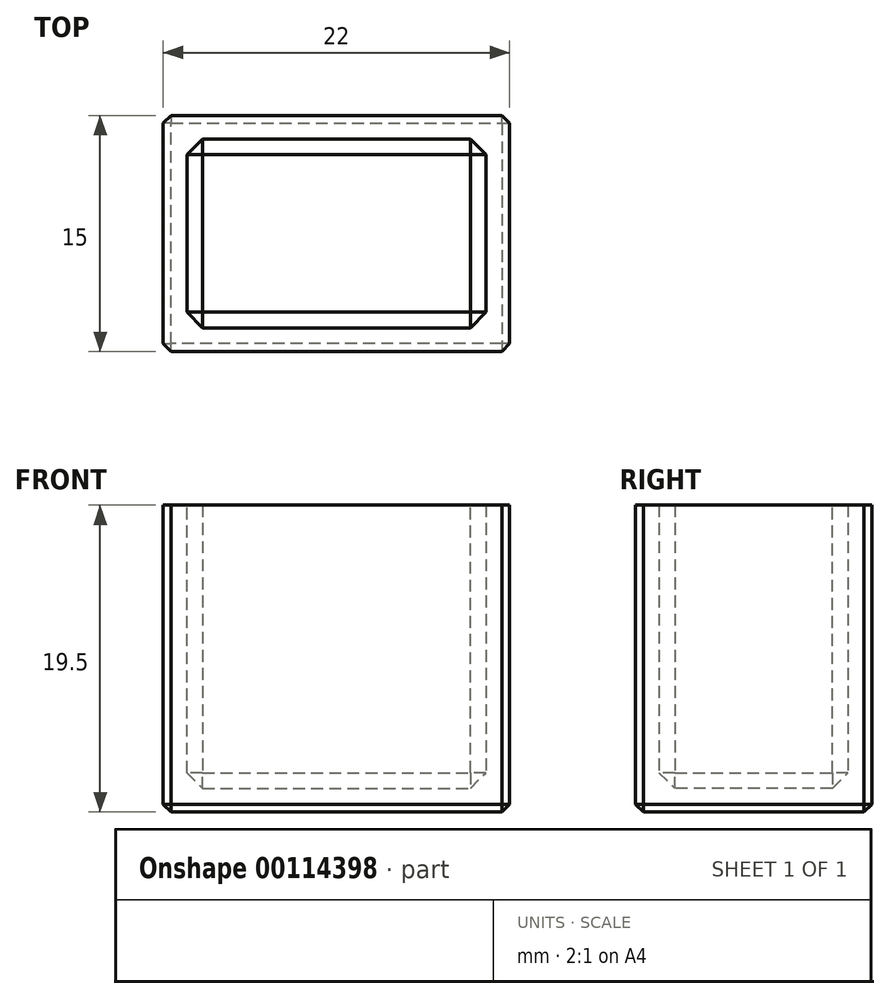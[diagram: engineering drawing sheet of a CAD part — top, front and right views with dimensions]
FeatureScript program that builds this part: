
annotation { "Feature Type Name" : "Feature", "Feature Type Description" : "" }
export const myFeature = defineFeature(function(context is Context, id is Id, definition is map)
    precondition{}
    {
        {
            var Q0;
            Q0=qCreatedBy(makeId("Top.planeOp"),FACE);
            var sketch = newSketch(context, id + "F0", { "sketchPlane" : qUnion([Q0])});
            skLineSegment(sketch, "E0.bottom", {"start": v(0, 0) * mm, "end": v(22, 0) * mm});
            skLineSegment(sketch, "E0.top", {"start": v(0, 15) * mm, "end": v(22, 15) * mm});
            skLineSegment(sketch, "E0.left", {"start": v(0, 0) * mm, "end": v(0, 15) * mm});
            skLineSegment(sketch, "E0.right", {"start": v(22, 0) * mm, "end": v(22, 15) * mm});
            skSolve(sketch);
        }
        {
            var Q0;
            Q0=makeQuery(id+"F0.imprint","IMPRINT",FACE,{"disambiguationData":[TD([[makeQuery(id+"F0.imprint","IMPRINT",EDGE,{"derivedFrom":sQuery(id+"F0.wireOp",EDGE,"E0.bottom")}),1.0]])]});
            extrude(context, id + "F1", {"entities" : qUnion([Q0]), "depth" : 1.5 * mm});
        }
        {
            var Q0;
            Q0=makeQuery(id+"F1.opExtrude","CAP_FACE",FACE,{"disambiguationData":[OSD([sQuery(id+"F0.wireOp",EDGE,"E0.bottom"),sQuery(id+"F0.wireOp",EDGE,"E0.top"),sQuery(id+"F0.wireOp",EDGE,"E0.left"),sQuery(id+"F0.wireOp",EDGE,"E0.right")])],"isStart":false});
            var sketch = newSketch(context, id + "F2", { "sketchPlane" : qUnion([Q0])});
            skLineSegment(sketch, "E1.0.0", {"start": v(0, 15) * mm, "end": v(0, 0) * mm});
            skLineSegment(sketch, "E1.0.1", {"start": v(0, 0) * mm, "end": v(22, 0) * mm});
            skLineSegment(sketch, "E1.0.2", {"start": v(22, 0) * mm, "end": v(22, 15) * mm});
            skLineSegment(sketch, "E1.0.3", {"start": v(22, 15) * mm, "end": v(0, 15) * mm});
            skLineSegment(sketch, "E2.0", {"start": v(1.5, 13.5) * mm, "end": v(1.5, 1.5) * mm});
            skLineSegment(sketch, "E2.1", {"start": v(20.5, 13.5) * mm, "end": v(1.5, 13.5) * mm});
            skLineSegment(sketch, "E2.2", {"start": v(20.5, 1.5) * mm, "end": v(20.5, 13.5) * mm});
            skLineSegment(sketch, "E2.3", {"start": v(1.5, 1.5) * mm, "end": v(20.5, 1.5) * mm});
            skSolve(sketch);
        }
        {
            var Q0;
            Q0 = qSketchRegion(id + "F2", true);
            extrude(context, id + "F3", {"entities" : qUnion([Q0]), "operationType" : NewBodyOperationType.ADD, "depth" : 18 * mm});
        }
        {
            var Q0;
            Q0=makeQuery(id+"F1.opExtrude","CAP_FACE",FACE,{"disambiguationData":[OSD([sQuery(id+"F0.wireOp",EDGE,"E0.bottom"),sQuery(id+"F0.wireOp",EDGE,"E0.top"),sQuery(id+"F0.wireOp",EDGE,"E0.left"),sQuery(id+"F0.wireOp",EDGE,"E0.right")])],"isStart":true});
            var Q1;
            Q1=makeQuery(id+"F3.boolean.opBoolean","MERGE",EDGE,{"derivedFrom":[makeQuery(id+"F1.opExtrude","SWEPT_EDGE",EDGE,{"disambiguationData":[OSD([sQuery(id+"F0.wireOp",EDGE,"E0.bottom"),sQuery(id+"F0.wireOp",EDGE,"E0.right")])]}),makeQuery(id+"F3.opExtrude","SWEPT_EDGE",EDGE,{"disambiguationData":[OSD([sQuery(id+"F2.wireOp",EDGE,"E1.0.1"),sQuery(id+"F2.wireOp",EDGE,"E1.0.2")])]})]});
            var Q2;
            Q2=makeQuery(id+"F3.boolean.opBoolean","MERGE",EDGE,{"derivedFrom":[makeQuery(id+"F1.opExtrude","SWEPT_EDGE",EDGE,{"disambiguationData":[OSD([sQuery(id+"F0.wireOp",EDGE,"E0.top"),sQuery(id+"F0.wireOp",EDGE,"E0.right")])]}),makeQuery(id+"F3.opExtrude","SWEPT_EDGE",EDGE,{"disambiguationData":[OSD([sQuery(id+"F2.wireOp",EDGE,"E1.0.2"),sQuery(id+"F2.wireOp",EDGE,"E1.0.3")])]})]});
            var Q3;
            Q3=makeQuery(id+"F3.boolean.opBoolean","MERGE",EDGE,{"derivedFrom":[makeQuery(id+"F1.opExtrude","SWEPT_EDGE",EDGE,{"disambiguationData":[OSD([sQuery(id+"F0.wireOp",EDGE,"E0.bottom"),sQuery(id+"F0.wireOp",EDGE,"E0.left")])]}),makeQuery(id+"F3.opExtrude","SWEPT_EDGE",EDGE,{"disambiguationData":[OSD([sQuery(id+"F2.wireOp",EDGE,"E1.0.0"),sQuery(id+"F2.wireOp",EDGE,"E1.0.1")])]})]});
            var Q4;
            Q4=makeQuery(id+"F3.boolean.opBoolean","MERGE",EDGE,{"derivedFrom":[makeQuery(id+"F1.opExtrude","SWEPT_EDGE",EDGE,{"disambiguationData":[OSD([sQuery(id+"F0.wireOp",EDGE,"E0.top"),sQuery(id+"F0.wireOp",EDGE,"E0.left")])]}),makeQuery(id+"F3.opExtrude","SWEPT_EDGE",EDGE,{"disambiguationData":[OSD([sQuery(id+"F2.wireOp",EDGE,"E1.0.0"),sQuery(id+"F2.wireOp",EDGE,"E1.0.3")])]})]});
            chamfer(context, id + "F4", {"entities" : qUnion([Q0, Q1, Q2, Q3, Q4]), "width" : 0.5 * mm, "tangentPropagation" : true});
        }
        {
            var Q0;
            Q0=makeQuery(id+"F1.opExtrude","CAP_FACE",FACE,{"disambiguationData":[OSD([sQuery(id+"F0.wireOp",EDGE,"E0.bottom"),sQuery(id+"F0.wireOp",EDGE,"E0.top"),sQuery(id+"F0.wireOp",EDGE,"E0.left"),sQuery(id+"F0.wireOp",EDGE,"E0.right")])],"isStart":false});
            var Q1;
            Q1=makeQuery(id+"F3.opExtrude","SWEPT_EDGE",EDGE,{"disambiguationData":[OSD([sQuery(id+"F2.wireOp",EDGE,"E2.1"),sQuery(id+"F2.wireOp",EDGE,"E2.2")])]});
            var Q2;
            Q2=makeQuery(id+"F3.opExtrude","SWEPT_EDGE",EDGE,{"disambiguationData":[OSD([sQuery(id+"F2.wireOp",EDGE,"E2.0"),sQuery(id+"F2.wireOp",EDGE,"E2.1")])]});
            var Q3;
            Q3=makeQuery(id+"F3.opExtrude","SWEPT_EDGE",EDGE,{"disambiguationData":[OSD([sQuery(id+"F2.wireOp",EDGE,"E2.0"),sQuery(id+"F2.wireOp",EDGE,"E2.3")])]});
            var Q4;
            Q4=makeQuery(id+"F3.opExtrude","SWEPT_EDGE",EDGE,{"disambiguationData":[OSD([sQuery(id+"F2.wireOp",EDGE,"E2.2"),sQuery(id+"F2.wireOp",EDGE,"E2.3")])]});
            chamfer(context, id + "F5", {"entities" : qUnion([Q0, Q1, Q2, Q3, Q4]), "width" : 1 * mm, "tangentPropagation" : true});
        }
    });
